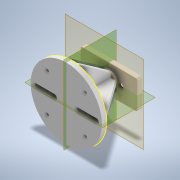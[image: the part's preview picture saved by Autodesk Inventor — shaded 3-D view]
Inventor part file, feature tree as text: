
AUTODESK INVENTOR PART (.ipt)
format: ipt  version: 2021 (Build 250183000, 183)  size: 393,728 bytes
history: native  units: mm
features: sketch x17, extrude x12, plane x6, reference x6, other x5, mirror x3, projected_geometry x2, loft x1, fillet x1
ambient origin geometry x8: Origin, YZ Plane, XZ Plane, XY Plane, X Axis, Y Axis, Z Axis, Center Point
bodies: Solid1 (feature_tree)
feature tree (53):
  extrude  "Extrusion1"  Depth=60.0mm
  extrude  "Extrusion2"  Depth=3.0mm TaperAngle=0.0deg
  sketch  "Sketch3"  dims[d6=3.0mm d7=0.0mm d8=1.4mm d9=0.0mm]
  plane  "Work Plane1"
  extrude  "Extrusion3"  Depth=1.4mm TaperAngle=0.0deg
  sketch  "Sketch4"  dims[d11=40.0mm d12=75.0mm]
  extrude  "Extrusion4"  Depth=75.0mm
  plane  "Work Plane3"
  extrude  "Extrusion5"  Depth=5.0mm TaperAngle=0.0deg
  sketch  "Sketch7"  dims[d22=8.0mm d23=38.0mm d24=0.0mm]
  sketch  "Sketch8"  dims[d26=38.0mm d27=0.0mm d28=75.0mm]
  loft  "Loft1"
  extrude  "Extrusion7"  Depth=38.0mm TaperAngle=0.0deg
  extrude  "Extrusion8"  Depth=75.0mm
  extrude  "Extrusion6"  Depth=75.0mm
  sketch  "Sketch12"  dims[d36=34.5mm d37=0.0mm d38=40.0mm d39=0.0mm]
  plane  "Work Plane4"
  extrude  "Extrusion9"  Depth=3.0mm
  plane  "Work Plane5"
  plane  "Work Plane6"
  mirror  "Mirror1"
  mirror  "Mirror2"
  sketch  "Sketch14"  dims[d44=10.0mm d45=0.0mm]
  extrude  "Extrusion10"  Depth=4.0mm
  fillet  "Fillet1"  Radius=3.0mm
  extrude  "Extrusion12"  Depth=40.0mm TaperAngle=0.0deg
  extrude  "Extrusion13"  Depth=2.0mm
  plane  "Work Plane7"
  mirror  "Mirror3"
  sketch  "Sketch1"  dims[d0=60.0mm d1=30.0mm]
  reference  "Reference1"
  sketch  "Sketch2"  dims[d2=2.0mm d3=0.0mm d4=3.0mm d5=0.0mm]
  reference  "Reference2"
  reference  "Reference3"
  reference  "Reference4"
  sketch  "Sketch5"  dims[d13=5.0mm d14=0.0mm d16=5.0mm d17=0.0mm]
  reference  "Reference5"
  reference  "Reference6"
  sketch  "Sketch6"  dims[d18=0.0mm d19=90.0deg d20=0.0mm d21=90.0deg]
  projected_geometry  "Projected Loop1"
  projected_geometry  "Projected Loop2"
  sketch  "Sketch9"  dims[d29=8.0mm d30=75.0mm]
  other  "Edges1"
  sketch  "Sketch10"  dims[d31=-40.0mm d32=3.0mm]
  sketch  "Sketch11"  dims[d33=4.0mm d34=4.0mm d35=3.0mm]
  sketch  "Sketch13"  dims[d40=19.0mm d43=2.0mm]
  sketch  "Sketch15"  dims[d46=10.0mm d47=0.0mm]
  sketch  "Sketch18"
  sketch  "Sketch19"
  other  "539636 HGP-16-A-B-SSK---(asm_0_-ZH).iam"
  other  "539636 HGP-16-A-B-SSK---(0_1_ZYL):1"
  other  "186717 ZBH-7:2"
  other  "186717 ZBH-7:1"
